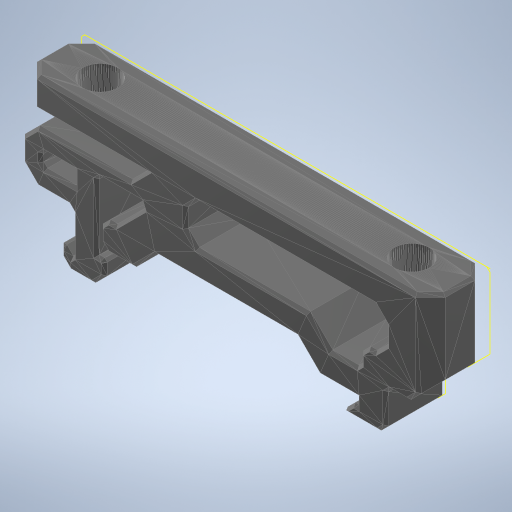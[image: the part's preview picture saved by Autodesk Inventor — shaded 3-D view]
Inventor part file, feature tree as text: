
AUTODESK INVENTOR PART (.ipt)
format: ipt  version: 2023 (Build 270158000, 158)  size: 299,008 bytes
history: native  units: in
note: dims shown in document units (in); Inventor stores cm internally (conversion verified against a paired STEP export)
features: other x2, sketch x1
ambient origin geometry x8: Origin, YZ Plane, XZ Plane, XY Plane, X Axis, Y Axis, Z Axis, Center Point
feature tree (3):
  other  "UHP_200_Mount_x2 (1)"
  sketch  "Sketch1"
  other  "MeshFeature1"
